# Revit family: TP Lite Dblt Door full height
name_source: partatom
category: Doors
revit_build: Autodesk Revit Architecture 2014 (Build: 20130308_1515(x64)
units: mm (PartAtom-declared; Revit-internal decimal feet)

## types (2) — shared parameters
Bottom Profile = Yes
Description = TP Lite
Door leaf offset = 3 mm  [stored 0.00984252 ft]
Door offset = 35 mm  [stored 0.114829 ft]
Function = Interior
Glass panel material = Triplan Glass
Handle Height = 977 mm  [stored 3.20538 ft]
Handle Horizontal Offest = 60 mm  [stored 0.19685 ft]
Profile material = Triplan Metal - Eloxeret Aluminium
URL = http://www.triplan.dk
zero-valued in all types: Door leaf Width, Explode object

## per-type parameters (varying)
| type | AcousticRating | Door Handle Type | Door leaf material | Door leaf thickness | Manufacturer | Thickness |
| Glass door |  | 2 | Triplan Glass | 10 mm  [stored 0.0328084 ft] | Triplan International A/S | 10 mm  [stored 0.0328084 ft] |
| Massive door | 25 RW dB | 1 | Triplan Door - NCS 0502Y | 40 mm  [stored 0.131234 ft] | Triplan International | 40 mm  [stored 0.131234 ft] |

note: [stored X ft] marks values corroborated as IEEE doubles in the binary element streams (Revit-internal decimal feet)

## geometry (parser evidence)
native form markers: Sweep x7
no freeform markers — native parametric forms only
